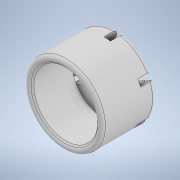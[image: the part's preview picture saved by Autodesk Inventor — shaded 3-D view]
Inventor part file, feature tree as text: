
AUTODESK INVENTOR PART (.ipt)
format: ipt  version: 2020 (Build 240168000, 168)  size: 313,856 bytes
history: native  units: in
note: dims shown in document units (in); Inventor stores cm internally (conversion verified against a paired STEP export)
features: sketch x8, extrude x7, fillet x6, chamfer x1
ambient origin geometry x8: Origin, YZ Plane, XZ Plane, XY Plane, X Axis, Y Axis, Z Axis, Center Point
bodies: Solid1 (feature_tree)
feature tree (22):
  extrude  "Extrusion1"  Depth=1.0in
  sketch  "Sketch2"  dims[d3=1.0in d4=0.0in d5=1.1in]
  extrude  "Extrusion2"  Depth=1.1in
  extrude  "Extrusion3"  Depth=0.125in
  fillet  "Fillet1"  Radius=0.125in
  fillet  "Fillet2"  Radius=0.05in
  fillet  "Fillet3"  Radius=0.05in
  fillet  "Fillet4"  Radius=0.2in
  extrude  "Extrusion4"  Depth=0.25in
  fillet  "Fillet5"  Radius=0.2in
  extrude  "Extrusion5"  Depth=0.1in
  fillet  "Fillet6"  Radius=2.3622in
  extrude  "Extrusion6"  Depth=0.5in
  extrude  "Extrusion7"  Depth=0.125in TaperAngle=45.0deg
  chamfer  "Chamfer1"  [1 undecoded]
  sketch  "Sketch1"  dims[d0=1.0in d1=0.0in d2=1.0in]
  sketch  "Sketch3"  dims[d6=0.2in d7=0.0in d8=0.125in d9=0.125in d10=0.05in d11=0.05in d12=0.2in d13=0.0in]
  sketch  "Sketch4"  dims[d14=0.05in d15=0.25in d16=0.2in d17=0.0in]
  sketch  "Sketch5"  dims[d18=0.05in d19=0.1in d20=2.3622in d22=360.0deg]
  sketch  "Sketch6"  dims[d24=1.0in d25=0.0in d26=0.5in]
  sketch  "Sketch7"  dims[d27=1.0in d28=0.0in d29=0.125in d30=0.125in d31=45.0deg]
  sketch  "Sketch8"
note: 1 required parameter value undecoded (feature->parameter linkage not recoverable at this tier; creation-order binding heuristic only, values carry confidence <= 0.55)
